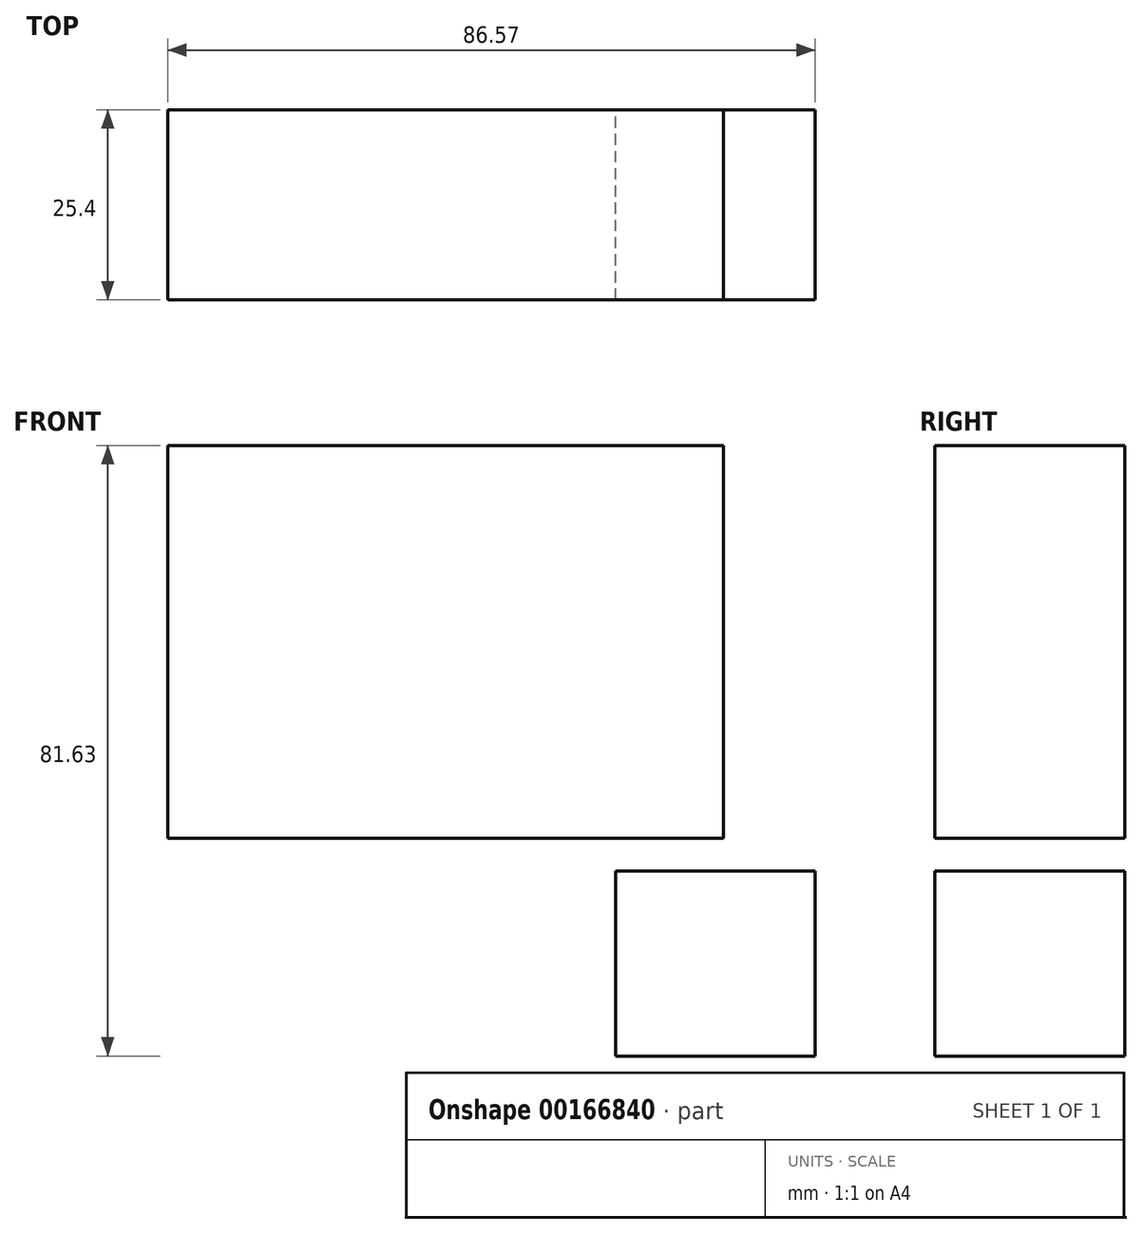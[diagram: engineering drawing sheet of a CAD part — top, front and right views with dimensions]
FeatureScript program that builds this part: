
annotation { "Feature Type Name" : "Feature", "Feature Type Description" : "" }
export const myFeature = defineFeature(function(context is Context, id is Id, definition is map)
    precondition{}
    {
        {
            var Q0;
            Q0=qCreatedBy(makeId("Front.planeOp"),FACE);
            var sketch = newSketch(context, id + "F0", { "sketchPlane" : qUnion([Q0])});
            skLineSegment(sketch, "E0.bottom", {"start": v(-14.37, 10.37) * mm, "end": v(12.27, 10.37) * mm});
            skLineSegment(sketch, "E0.top", {"start": v(-14.37, -14.37) * mm, "end": v(12.27, -14.37) * mm});
            skLineSegment(sketch, "E0.left", {"start": v(-14.37, 10.37) * mm, "end": v(-14.37, -14.37) * mm});
            skLineSegment(sketch, "E0.right", {"start": v(12.27, 10.37) * mm, "end": v(12.27, -14.37) * mm});
            skLineSegment(sketch, "E1.bottom", {"start": v(0, 14.75) * mm, "end": v(-74.3, 14.75) * mm});
            skLineSegment(sketch, "E1.top", {"start": v(0, 67.26) * mm, "end": v(-74.3, 67.26) * mm});
            skLineSegment(sketch, "E1.left", {"start": v(0, 14.75) * mm, "end": v(0, 67.26) * mm});
            skLineSegment(sketch, "E1.right", {"start": v(-74.3, 14.75) * mm, "end": v(-74.3, 67.26) * mm});
            skSolve(sketch);
        }
        {
            var Q0;
            Q0 = qSketchRegion(id + "F0", true);
            extrude(context, id + "F1", {"entities" : qUnion([Q0]), "depth" : 25.4 * mm});
        }
    });
